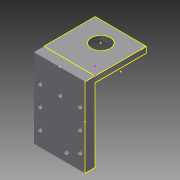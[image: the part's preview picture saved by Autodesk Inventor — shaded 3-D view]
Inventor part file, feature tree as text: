
AUTODESK INVENTOR PART (.ipt)
format: ipt  version: 2013 (Build 170138000, 138)  size: 174,080 bytes
history: native  units: mm
features: hole x13, sketch x8, extrude x3
ambient origin geometry x8: Origin, YZ Plane, XZ Plane, XY Plane, X Axis, Y Axis, Z Axis, Center Point
bodies: Solid1 (feature_tree)
feature tree (24):
  extrude  "Extrusion1"  Depth=88.392mm
  hole  "Hole1"  [1 undecoded]
  hole  "Hole3"  [1 undecoded]
  hole  "Hole4"  [1 undecoded]
  hole  "Hole5"  [1 undecoded]
  hole  "Hole6"  [1 undecoded]
  hole  "Hole7"  [1 undecoded]
  hole  "Hole8"  [1 undecoded]
  extrude  "Extrusion2"  [1 undecoded]
  hole  "Hole9"  [1 undecoded]
  extrude  "Extrusion3"  [1 undecoded]
  hole  "Hole10"  [1 undecoded]
  hole  "Hole13"  [1 undecoded]
  hole  "Hole14"  [1 undecoded]
  sketch  "Sketch4"  dims[d22=7.112mm d23=7.112mm d24=6.7564mm d25=19.05mm d26=12.8778mm d27=6.35mm d28=14.3117mm d29=25.4mm d30=20.594885mm]
  sketch  "Sketch5"  dims[d31=7.112mm d32=32.512mm d33=6.7564mm d34=19.05mm d35=12.8778mm d36=6.35mm d37=14.3117mm d38=25.4mm d39=20.594885mm]
  sketch  "Sketch6"  dims[d40=57.912mm d41=7.112mm d42=6.7564mm d43=19.05mm d44=12.8778mm d45=6.35mm d46=14.3117mm d47=25.4mm d48=20.594885mm]
  sketch  "Sketch7"  dims[d49=57.912mm d50=32.512mm d51=6.7564mm d52=19.05mm d53=12.8778mm d54=6.35mm d55=14.3117mm d56=25.4mm d57=20.594885mm]
  sketch  "Sketch8"  dims[d58=7.112mm d59=57.912mm d60=6.7564mm d61=19.05mm d62=12.8778mm d63=6.35mm d64=14.3117mm d65=25.4mm d66=20.594885mm d67=7.112mm d68=32.512mm d69=6.7564mm d70=19.05mm d71=12.8778mm d72=6.35mm d73=14.3117mm d74=25.4mm d75=20.594885mm d77=65.278mm d78=0.0mm d79=32.512mm d80=25.4mm d81=23.9268mm d82=19.05mm d83=12.8778mm d84=6.35mm d85=14.3117mm d86=25.4mm d87=20.594885mm d88=12.7mm d89=0.0mm d90=24.4348mm d91=11.729974mm d92=4.318mm d93=19.05mm d94=7.112mm d95=5.588mm d96=14.3117mm d97=25.4mm d98=20.594885mm d117=19.812mm d118=57.531mm d119=4.9784mm d120=19.05mm d121=12.8778mm d122=6.35mm d123=14.3117mm d124=7.62mm d125=20.594885mm d126=19.812mm d127=57.531mm d128=4.9784mm d129=19.05mm d130=12.8778mm d131=6.35mm d132=14.3117mm d133=7.62mm d134=20.594885mm d144=19.812mm d145=32.131mm d146=4.9784mm d147=19.05mm d148=9.525mm d149=6.35mm d150=14.3117mm d151=7.62mm d152=20.594885mm d153=45.212mm d154=32.131mm d155=4.9784mm d156=19.05mm d157=9.525mm d158=6.35mm d159=14.3117mm d160=7.62mm d161=20.594885mm]
  hole  "Hole16"  [1 undecoded]
  hole  "Hole17"  [1 undecoded]
  sketch  "Sketch1"  dims[d0=65.024mm d1=88.392mm]
  sketch  "Sketch2"  dims[d2=12.7mm d3=0.0mm]
  sketch  "Sketch3"  dims[d4=7.112mm d5=7.112mm d6=6.7564mm d7=19.05mm d8=12.8778mm d9=6.35mm d10=14.3117mm d11=25.4mm d12=20.594885mm]
note: 15 required parameter values undecoded (feature->parameter linkage not recoverable at this tier; creation-order binding heuristic only, values carry confidence <= 0.55)
